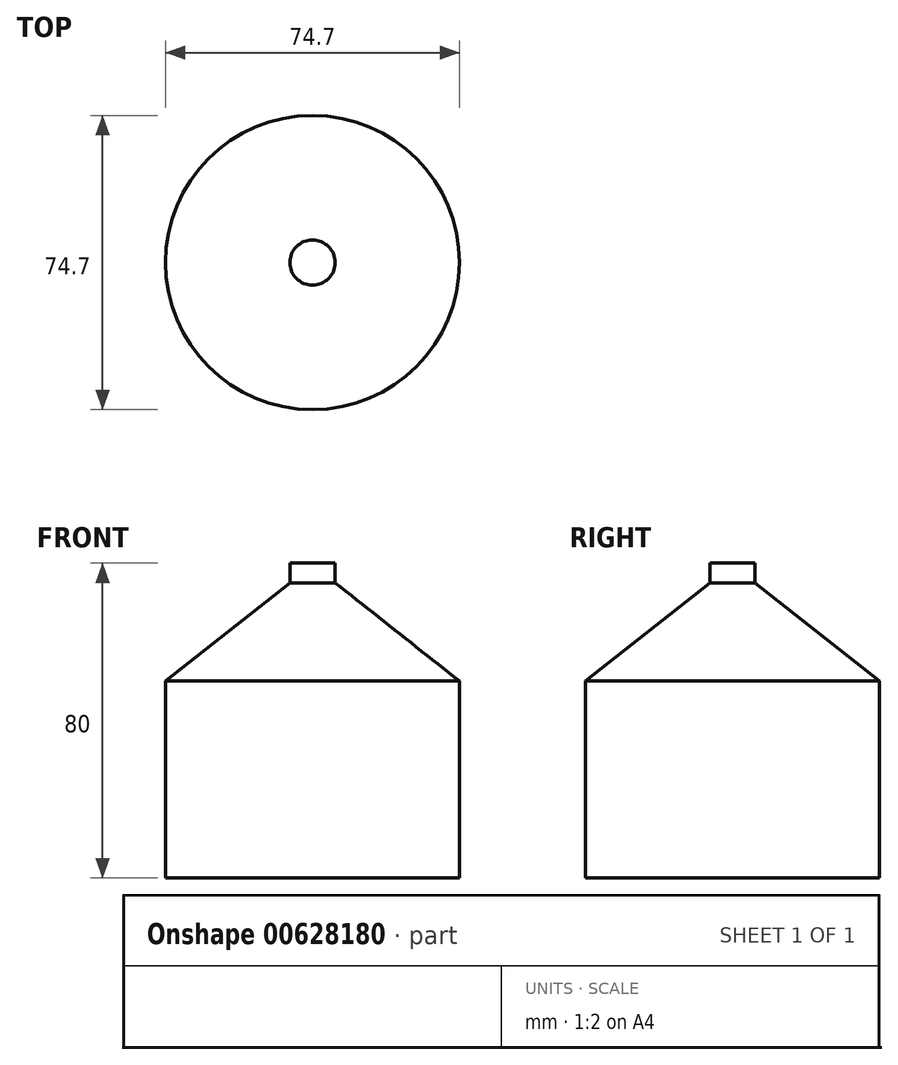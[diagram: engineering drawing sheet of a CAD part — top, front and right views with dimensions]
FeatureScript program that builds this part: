
annotation { "Feature Type Name" : "Feature", "Feature Type Description" : "" }
export const myFeature = defineFeature(function(context is Context, id is Id, definition is map)
    precondition{}
    {
        {
            var Q0;
            Q0=qCreatedBy(makeId("Top.planeOp"),FACE);
            var sketch = newSketch(context, id + "F0", { "sketchPlane" : qUnion([Q0])});
            skCircle(sketch, "E0", {"center": v(0, 0) * mm, "radius": 37.35 * mm});
            skSolve(sketch);
        }
        {
            var Q0;
            Q0=makeQuery(id+"F0.imprint","IMPRINT",FACE,{"disambiguationData":[TD([[makeQuery(id+"F0.imprint","IMPRINT",EDGE,{"derivedFrom":sQuery(id+"F0.wireOp",EDGE,"E0")}),1.0]])]});
            extrude(context, id + "F1", {"entities" : qUnion([Q0]), "depth" : 50 * mm, "offsetDistance" : 25 * mm});
        }
        {
            var Q0;
            Q0=qCreatedBy(makeId("Top.planeOp"),FACE);
            cPlane(context, id + "F2", {"entities" : qUnion([Q0]), "cplaneType" : CPlaneType.OFFSET, "offset" : 75 * mm, "width" : 150 * mm, "height" : 150 * mm});
        }
        {
            var Q0;
            Q0=qCreatedBy(id+"F2.planeOp",FACE);
            var sketch = newSketch(context, id + "F3", { "sketchPlane" : qUnion([Q0])});
            skCircle(sketch, "E1", {"center": v(0, 0) * mm, "radius": 5.73 * mm});
            skSolve(sketch);
        }
        {
            var Q1;
            Q1=makeQuery(id+"F1.opExtrude","CAP_FACE",FACE,{"disambiguationData":[OSD([sQuery(id+"F0.wireOp",EDGE,"E0")])],"isStart":false});
            var Q2;
            Q2=makeQuery(id+"F3.imprint","IMPRINT",FACE,{"disambiguationData":[TD([[makeQuery(id+"F3.imprint","IMPRINT",EDGE,{"derivedFrom":sQuery(id+"F3.wireOp",EDGE,"E1")}),1.0]])]});
            loft(context, id + "F4", {"operationType" : NewBodyOperationType.ADD, "sheetProfilesArray" : [{ "sheetProfileEntities" : qUnion([Q1]) }, { "sheetProfileEntities" : qUnion([Q2]) }]});
        }
        {
            var Q0;
            Q0=makeQuery(id+"F4.opLoft","CAP_FACE",FACE,{"disambiguationData":[OSD([makeQuery(id+"F3.imprint","IMPRINT",FACE,{"disambiguationData":[TD([[makeQuery(id+"F3.imprint","IMPRINT",EDGE,{"derivedFrom":sQuery(id+"F3.wireOp",EDGE,"E1")}),1.0]])]})])],"isStart":true});
            extrude(context, id + "F5", {"entities" : qUnion([Q0]), "operationType" : NewBodyOperationType.ADD, "depth" : 5 * mm, "offsetDistance" : 25 * mm});
        }
    });
